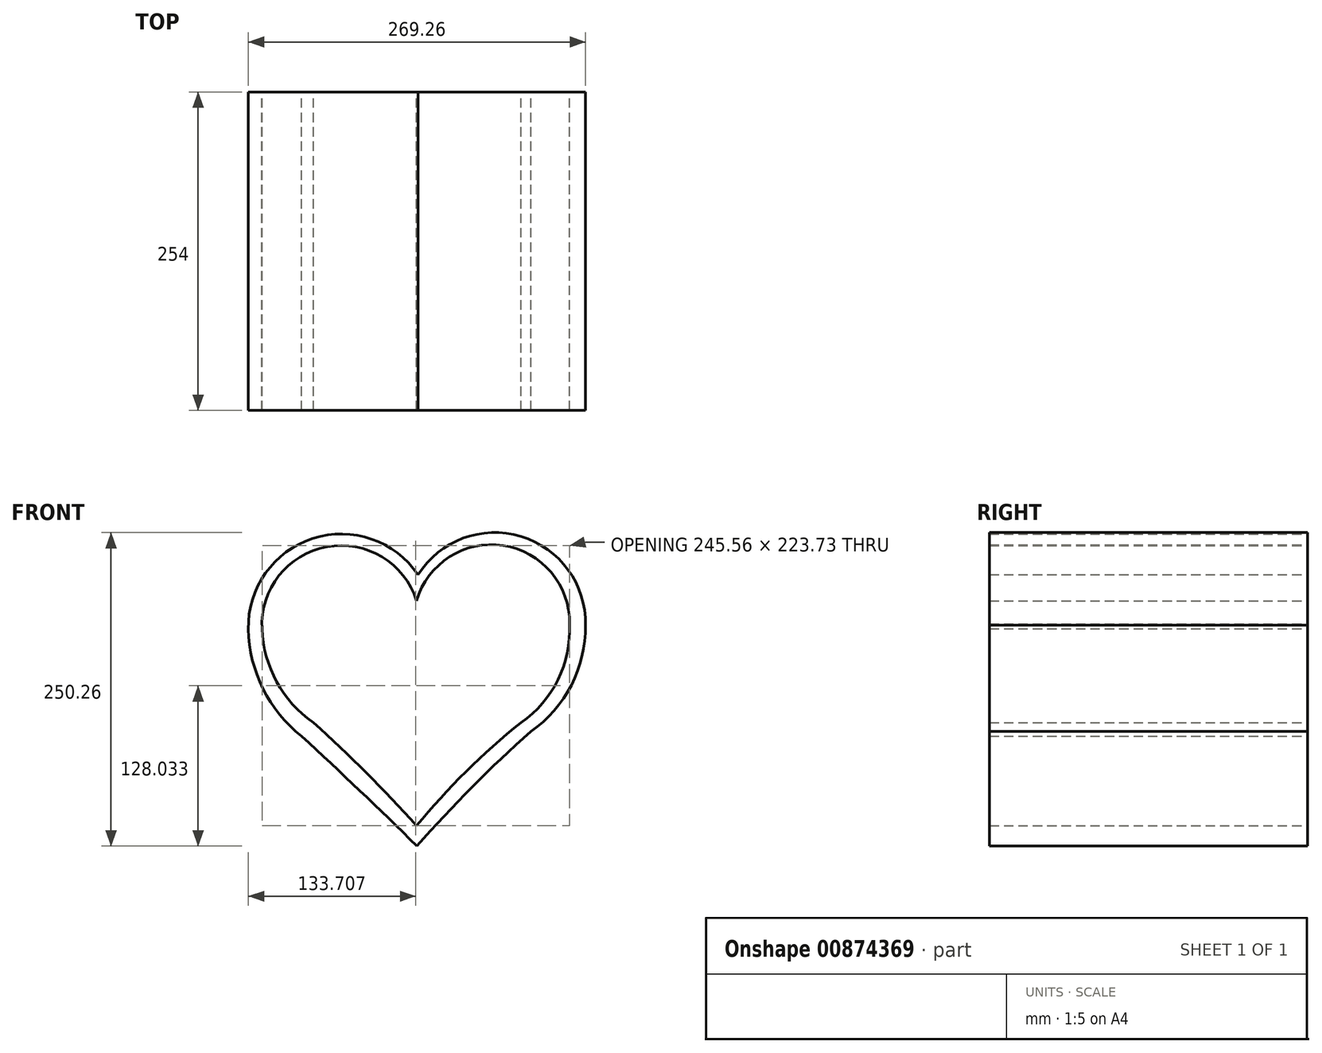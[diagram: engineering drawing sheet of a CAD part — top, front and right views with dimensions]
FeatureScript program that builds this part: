
annotation { "Feature Type Name" : "Feature", "Feature Type Description" : "" }
export const myFeature = defineFeature(function(context is Context, id is Id, definition is map)
    precondition{}
    {
        {
            var Q0;
            Q0=qCreatedBy(makeId("Front.planeOp"),FACE);
            var sketch = newSketch(context, id + "F0", { "sketchPlane" : qUnion([Q0])});
            skArc(sketch, "E0", {"start": v(256.47, 177.15) * mm, "mid": v(203.47, 239.9) * mm, "end": v(134.23, 195.7) * mm});
            skArc(sketch, "E1", {"start": v(217.72, 98.57) * mm, "mid": v(247.27, 132.84) * mm, "end": v(256.47, 177.15) * mm});
            skArc(sketch, "E2", {"start": v(134.23, 195.7) * mm, "mid": v(62.71, 238.85) * mm, "end": v(10.9, 173.33) * mm});
            skArc(sketch, "E3", {"start": v(10.9, 173.33) * mm, "mid": v(22.57, 131.13) * mm, "end": v(51.83, 98.57) * mm});
            skArc(sketch, "E4", {"start": v(134.23, 16.17) * mm, "mid": v(94.2, 58.53) * mm, "end": v(51.83, 98.57) * mm});
            skArc(sketch, "E5", {"start": v(217.72, 98.57) * mm, "mid": v(173.84, 59.53) * mm, "end": v(134.23, 16.17) * mm});
            skArc(sketch, "E6", {"start": v(269.23, 176.3) * mm, "mid": v(217.61, 247.18) * mm, "end": v(135.44, 216.59) * mm});
            skArc(sketch, "E7", {"start": v(135.44, 216.59) * mm, "mid": v(51.44, 245.53) * mm, "end": v(0, 173.08) * mm});
            skArc(sketch, "E8", {"start": v(0, 173.08) * mm, "mid": v(11.64, 125.6) * mm, "end": v(42.52, 87.67) * mm});
            skArc(sketch, "E9", {"start": v(134.61, 0) * mm, "mid": v(88.97, 44.26) * mm, "end": v(42.52, 87.67) * mm});
            skArc(sketch, "E10", {"start": v(225.57, 91.5) * mm, "mid": v(257.9, 128.5) * mm, "end": v(269.23, 176.3) * mm});
            skArc(sketch, "E11", {"start": v(225.57, 91.5) * mm, "mid": v(178.7, 47.13) * mm, "end": v(134.61, 0) * mm});
            skSolve(sketch);
        }
        {
            var Q0;
            Q0=makeQuery(id+"F0.imprint","IMPRINT",FACE,{"disambiguationData":[TD([[makeQuery(id+"F0.imprint","IMPRINT",EDGE,{"derivedFrom":sQuery(id+"F0.wireOp",EDGE,"E0")}),-1.0]])]});
            extrude(context, id + "F1", {"entities" : qUnion([Q0]), "depth" : 254 * mm, "offsetDistance" : 25.4 * mm});
        }
    });
